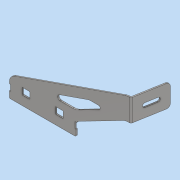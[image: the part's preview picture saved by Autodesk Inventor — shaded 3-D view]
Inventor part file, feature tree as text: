
AUTODESK INVENTOR PART (.ipt)
format: ipt  version: 2020 (Build 240168000, 168)  size: 425,984 bytes
history: native  units: mm
features: other x3, extrude x1, plane x1
ambient origin geometry x8: Origin, YZ Plane, XZ Plane, XY Plane, X Axis, Y Axis, Z Axis, Center Point
bodies: Body1 (feature_tree)
feature tree (5):
  other  "實體1"
  extrude  "擠出1"  Depth=130.0mm
  other  "折彎零件1"
  plane  "工作平面1"
  other  "定義1"
